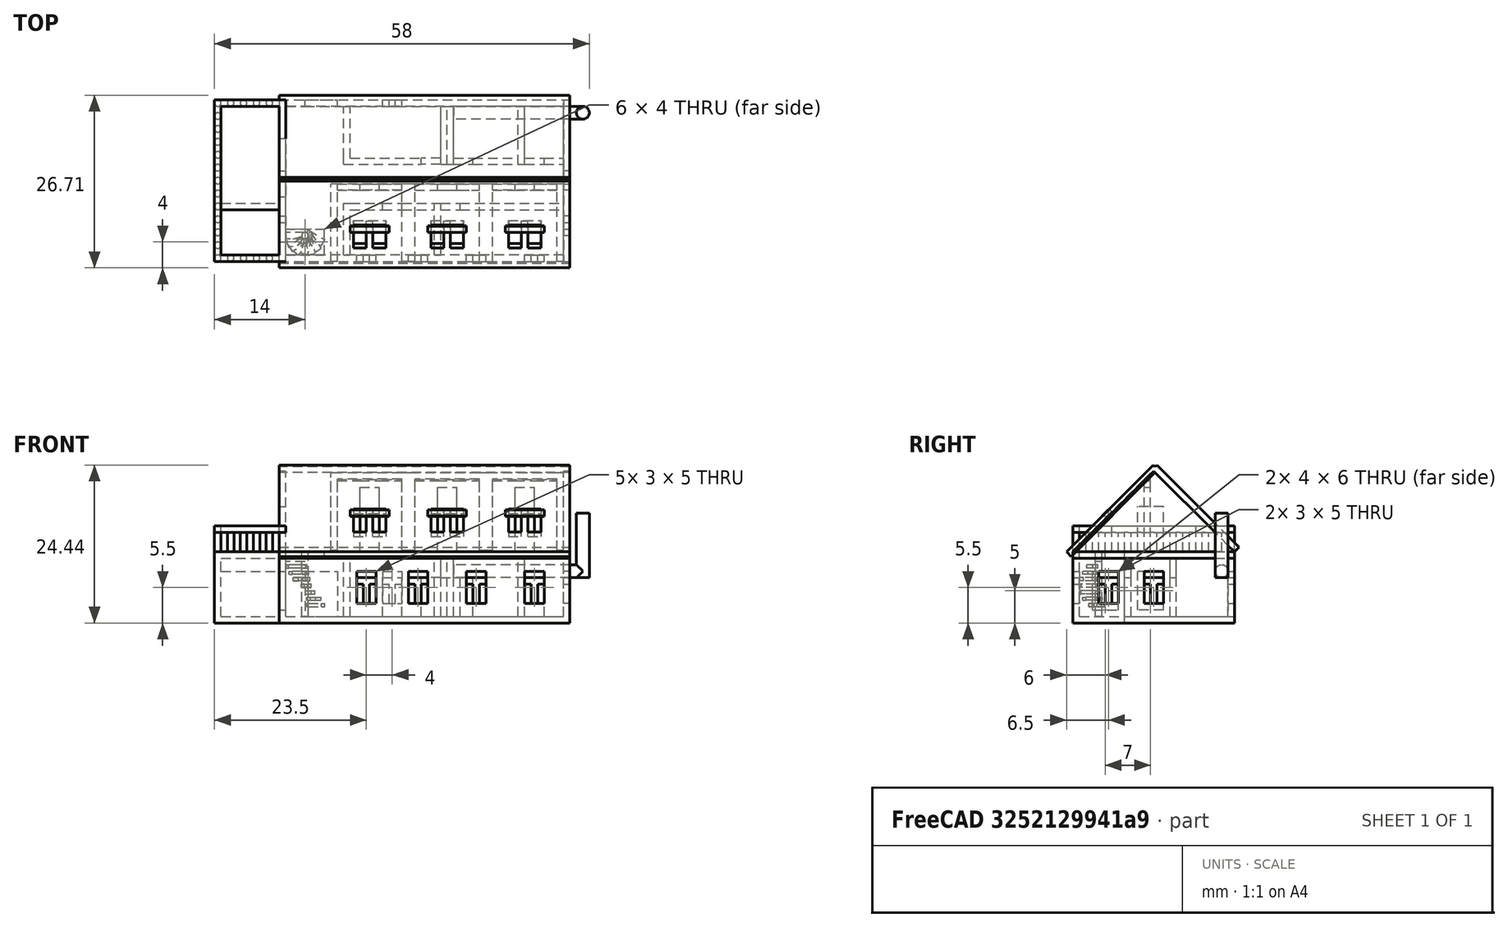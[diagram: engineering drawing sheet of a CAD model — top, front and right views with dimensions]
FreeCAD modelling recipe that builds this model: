
FCSTD DOCUMENT  (FreeCAD 0.18R4 (GitTag))
Label: House
License: All rights reserved
LicenseURL: http://en.wikipedia.org/wiki/All_rights_reserved
objects: Part::Box×102, Part::MultiFuse×56, Part::Cut×28, Part::Cylinder×25
note: 211 computed .brp shape members not serialized (recipe doc carries the construction recipe); baked Part::Feature solids carry a one-line shape summary decoded from their .brp

FEATURE [Part::Box] Box001  label="Куб001"
  AttacherType = Attacher::AttachEngine3D
  Height = 10
  Length = 45
  Width = 25
FEATURE [Part::Box] Box  label="Куб"
  AttacherType = Attacher::AttachEngine3D
  Height = 10
  Length = 43
  Placement = pos=(1,1,1) rot=(0,0,1;0rad)
  Width = 23
FEATURE [Part::Cut] Cut
  Base = -> Box001
  Tool = -> Box
FEATURE [Part::Box] Box002  label="Куб002"
  AttacherType = Attacher::AttachEngine3D
  Height = 9
  Length = 1
  Placement = pos=(16,15,1) rot=(0,0,1;0rad)
  Width = 9
FEATURE [Part::Box] Box003  label="Куб003"
  AttacherType = Attacher::AttachEngine3D
  Height = 9
  Length = 12
  Placement = pos=(1,15,1) rot=(0,0,1;0rad)
  Width = 1
FEATURE [Part::Box] Box004  label="Куб004"
  AttacherType = Attacher::AttachEngine3D
  Height = 3
  Length = 1
  Placement = pos=(16,15,7) rot=(0,0,1;1.5708rad)
  Width = 3
FEATURE [Part::Box] Box005  label="Куб005"
  AttacherType = Attacher::AttachEngine3D
  Height = 11
  Length = 8
  Placement = pos=(-9,0,0) rot=(0,0,1;1.5708rad)
  Width = 1
FEATURE [Part::Box] Box006  label="Куб006"
  AttacherType = Attacher::AttachEngine3D
  Height = 11
  Length = 9
  Placement = pos=(-9,0,0) rot=(0,0,1;0rad)
  Width = 1
FEATURE [Part::Box] Box007  label="Куб007"
  AttacherType = Attacher::AttachEngine3D
  Height = 9
  Length = 1
  Placement = pos=(10,1,1) rot=(0,0,1;0rad)
  Width = 8
FEATURE [Part::Box] Box008  label="Куб008"
  AttacherType = Attacher::AttachEngine3D
  Height = 9
  Length = 1
  Placement = pos=(24,1,1) rot=(0,0,1;0rad)
  Width = 8
FEATURE [Part::Box] Box009  label="Куб009"
  AttacherType = Attacher::AttachEngine3D
  Height = 9
  Length = 16
  Placement = pos=(28,8,1) rot=(0,0,1;0rad)
  Width = 1
FEATURE [Part::Box] Box010  label="Куб010"
  AttacherType = Attacher::AttachEngine3D
  Height = 3
  Length = 3
  Placement = pos=(25,8,7) rot=(0,0,1;0rad)
  Width = 1
FEATURE [Part::Box] Box011  label="Куб011"
  AttacherType = Attacher::AttachEngine3D
  Height = 9
  Length = 7
  Placement = pos=(37,15,1) rot=(0,0,1;0rad)
  Width = 1
FEATURE [Part::Box] Box012  label="Куб012"
  AttacherType = Attacher::AttachEngine3D
  Height = 9
  Length = 1
  Placement = pos=(33,15,1) rot=(0,0,1;0rad)
  Width = 9
FEATURE [Part::Box] Box013  label="Куб013"
  AttacherType = Attacher::AttachEngine3D
  Height = 3
  Length = 3
  Placement = pos=(34,15,7) rot=(0,0,1;0rad)
  Width = 1
FEATURE [Part::MultiFuse] Fusion003
  Placement = pos=(-7,0,0) rot=(0,0,1;0rad)
  Shapes = -> [Box013,Box012,Box011]
FEATURE [Part::MultiFuse] Fusion005
  Shapes = -> [Box010,Box008,Box009]
FEATURE [Part::Box] Box014  label="Куб014"
  AttacherType = Attacher::AttachEngine3D
  Height = 9
  Length = 3
  Placement = pos=(30,15,1) rot=(0,0,1;0rad)
  Width = 1
FEATURE [Part::Box] Box015  label="Куб015"
  AttacherType = Attacher::AttachEngine3D
  Height = 9
  Length = 1
  Placement = pos=(26,15,1) rot=(0,0,1;0rad)
  Width = 9
FEATURE [Part::Box] Box016  label="Куб016"
  AttacherType = Attacher::AttachEngine3D
  Height = 3
  Length = 3
  Placement = pos=(27,15,7) rot=(0,0,1;0rad)
  Width = 1
FEATURE [Part::Box] Box017  label="Куб017"
  AttacherType = Attacher::AttachEngine3D
  Height = 9
  Length = 5
  Placement = pos=(11,8,1) rot=(0,0,1;0rad)
  Width = 1
FEATURE [Part::Box] Box018  label="Куб018"
  AttacherType = Attacher::AttachEngine3D
  Height = 9
  Length = 5
  Placement = pos=(19,8,1) rot=(0,0,1;0rad)
  Width = 1
FEATURE [Part::Box] Box019  label="Куб019"
  AttacherType = Attacher::AttachEngine3D
  Height = 3
  Length = 3
  Placement = pos=(16,8,7) rot=(0,0,1;0rad)
  Width = 1
FEATURE [Part::MultiFuse] Fusion007
  Shapes = -> [Box019,Box018,Box017]
FEATURE [Part::Box] Box020  label="Куб020"
  AttacherType = Attacher::AttachEngine3D
  Height = 6
  Length = 6
  Placement = pos=(-2,10,2) rot=(0,0,1;0rad)
  Width = 4
FEATURE [Part::Cut] Cut001
  Base = -> Cut
  Tool = -> Box020
FEATURE [Part::Box] Box021  label="Куб021"
  AttacherType = Attacher::AttachEngine3D
  Height = 9
  Length = 10
  Placement = pos=(-10,8,0) rot=(0,0,1;0rad)
  Width = 1
FEATURE [Part::Box] Box022  label="Куб022"
  AttacherType = Attacher::AttachEngine3D
  Height = 9
  Length = 1
  Placement = pos=(-10,9,0) rot=(0,0,1;0rad)
  Width = 16
FEATURE [Part::Box] Box024  label="Куб024"
  AttacherType = Attacher::AttachEngine3D
  Height = 2
  Length = 9
  Placement = pos=(-9,24,7) rot=(0,0,1;0rad)
  Width = 1
FEATURE [Part::Box] Box025  label="Куб025"
  AttacherType = Attacher::AttachEngine3D
  Height = 1
  Length = 10
  Placement = pos=(-10,8,9) rot=(0,0,1;0rad)
  Width = 17
FEATURE [Part::MultiFuse] Fusion010
  Placement = pos=(0,0,1) rot=(0,0,1;0rad)
  Shapes = -> [Box025,Box024,Box022,Box021]
FEATURE [Part::Box] Box026  label="Куб026"
  AttacherType = Attacher::AttachEngine3D
  Height = 7
  Length = 5
  Placement = pos=(4,20,1) rot=(0,0,1;0rad)
  Width = 7
FEATURE [Part::MultiFuse] Fusion
  Placement = pos=(11,0,0) rot=(0,0,1;0rad)
  Shapes = -> [Box014,Box016,Box015]
FEATURE [Part::Box] Box027  label="Куб027"
  AttacherType = Attacher::AttachEngine3D
  Height = 1
  Length = 45
  Placement = pos=(0,0,10) rot=(0,0,1;0rad)
  Width = 25
FEATURE [Part::Box] Box028  label="Куб028"
  AttacherType = Attacher::AttachEngine3D
  Height = 13
  Length = 1
  Placement = pos=(0,0,11) rot=(0,0,1;0rad)
  Width = 25
FEATURE [Part::Box] Box029  label="Куб029"
  AttacherType = Attacher::AttachEngine3D
  Height = 10
  Length = 10
  Placement = pos=(-9,0,11) rot=(1,0,0;0.785398rad)
  Width = 20
FEATURE [Part::Box] Box030  label="Куб030"
  AttacherType = Attacher::AttachEngine3D
  Height = 20
  Length = 10
  Placement = pos=(-9,25,11) rot=(1,0,0;0.785398rad)
  Width = 10
FEATURE [Part::Cut] Cut003
  Base = -> Box028
  Tool = -> Box029
FEATURE [Part::Cut] Cut004
  Base = -> Cut003
  Tool = -> Box030
FEATURE [Part::Box] Box031  label="Куб031"
  AttacherType = Attacher::AttachEngine3D
  Height = 13
  Length = 1
  Placement = pos=(0,0,11) rot=(0,0,1;0rad)
  Width = 25
FEATURE [Part::Box] Box032  label="Куб032"
  AttacherType = Attacher::AttachEngine3D
  Height = 10
  Length = 10
  Placement = pos=(-9,0,11) rot=(1,0,0;0.785398rad)
  Width = 20
FEATURE [Part::Box] Box033  label="Куб033"
  AttacherType = Attacher::AttachEngine3D
  Height = 20
  Length = 10
  Placement = pos=(-9,25,11) rot=(1,0,0;0.785398rad)
  Width = 10
FEATURE [Part::Box] Box034  label="Куб034"
  AttacherType = Attacher::AttachEngine3D
  Height = 19
  Length = 45
  Placement = pos=(0,-1,11) rot=(-1,0,0;0.785398rad)
  Width = 1
FEATURE [Part::Box] Box035  label="Куб035"
  AttacherType = Attacher::AttachEngine3D
  Height = 18
  Length = 45
  Placement = pos=(0,25,11) rot=(1,0,0;0.785398rad)
  Width = 1
FEATURE [Part::Box] Box036  label="Куб036"
  AttacherType = Attacher::AttachEngine3D
  Height = 1
  Length = 6
  Placement = pos=(1,1,10) rot=(0,0,1;0rad)
  Width = 4
FEATURE [Part::Box] Box052  label="Куб052"
  AttacherType = Attacher::AttachEngine3D
  Height = 1
  Length = 10
  Placement = pos=(-10,8,0) rot=(0,0,1;0rad)
  Width = 17
FEATURE [Part::MultiFuse] Fusion024
  Shapes = -> [Fusion010,Box052]
FEATURE [Part::Box] Box056  label="Куб056"
  AttacherType = Attacher::AttachEngine3D
  Height = 5
  Length = 3
  Placement = pos=(16,20,3) rot=(0,0,1;0rad)
  Width = 6
FEATURE [Part::Box] Box058  label="Куб058"
  AttacherType = Attacher::AttachEngine3D
  Height = 5
  Length = 3
  Placement = pos=(12,-2,3) rot=(0,0,1;0rad)
  Width = 6
FEATURE [Part::Box] Box059  label="Куб059"
  AttacherType = Attacher::AttachEngine3D
  Height = 5
  Length = 3
  Placement = pos=(20,-2,3) rot=(0,0,1;0rad)
  Width = 6
FEATURE [Part::Box] Box060  label="Куб060"
  AttacherType = Attacher::AttachEngine3D
  Height = 5
  Length = 3
  Placement = pos=(29,-2,3) rot=(0,0,1;0rad)
  Width = 6
FEATURE [Part::Box] Box061  label="Куб061"
  AttacherType = Attacher::AttachEngine3D
  Height = 5
  Length = 3
  Placement = pos=(38,-2,3) rot=(0,0,1;0rad)
  Width = 6
FEATURE [Part::Box] Box062  label="Куб062"
  AttacherType = Attacher::AttachEngine3D
  Height = 5
  Length = 3
  Placement = pos=(46,4,3) rot=(0,0,1;1.5708rad)
  Width = 6
FEATURE [Part::Box] Box063  label="Куб063"
  AttacherType = Attacher::AttachEngine3D
  Height = 5
  Length = 3
  Placement = pos=(46,11,3) rot=(0,0,1;1.5708rad)
  Width = 6
FEATURE [Part::Cylinder] Cylinder001  label="Цилиндр001"
  Angle = 360
  AttacherType = Attacher::AttachEngine3D
  Height = 21
  Placement = pos=(48,23,8) rot=(0,-1,0;1.5708rad)
  Radius = 1
FEATURE [Part::Cylinder] Cylinder002  label="Цилиндр002"
  Angle = 360
  AttacherType = Attacher::AttachEngine3D
  Height = 9
  Placement = pos=(47,23,7) rot=(0,0,1;0rad)
  Radius = 1
FEATURE [Part::Cylinder] Cylinder003  label="Цилиндр003"
  Angle = 360
  AttacherType = Attacher::AttachEngine3D
  Height = 10
  Placement = pos=(47,23,7) rot=(0,0,1;0rad)
  Radius = 1
FEATURE [Part::Cut] Cut021
  Base = -> Cylinder001
  Tool = -> Cylinder002
FEATURE [Part::Box] Box064  label="Куб064"
  AttacherType = Attacher::AttachEngine3D
  Height = 10
  Length = 10
  Placement = pos=(47,14,0) rot=(0,0,1;0rad)
  Width = 10
FEATURE [Part::Cut] Cut022
  Base = -> Cut021
  Tool = -> Box064
FEATURE [Part::MultiFuse] Fusion025
  Shapes = -> [Cylinder003,Cut022]
FEATURE [Part::Box] Box066  label="Куб066"
  AttacherType = Attacher::AttachEngine3D
  Height = 1
  Length = 3
  Placement = pos=(12,0,6) rot=(0,0,1;0rad)
  Width = 1
FEATURE [Part::Box] Box067  label="Куб067"
  AttacherType = Attacher::AttachEngine3D
  Height = 1
  Length = 3
  Placement = pos=(20,0,6) rot=(0,0,1;0rad)
  Width = 1
FEATURE [Part::Box] Box068  label="Куб068"
  AttacherType = Attacher::AttachEngine3D
  Height = 1
  Length = 3
  Placement = pos=(29,0,6) rot=(0,0,1;0rad)
  Width = 1
FEATURE [Part::Box] Box069  label="Куб069"
  AttacherType = Attacher::AttachEngine3D
  Height = 1
  Length = 3
  Placement = pos=(38,0,6) rot=(0,0,1;0rad)
  Width = 1
FEATURE [Part::Box] Box071  label="Куб071"
  AttacherType = Attacher::AttachEngine3D
  Height = 3
  Length = 1
  Placement = pos=(13,0,3) rot=(0,0,1;0rad)
  Width = 1
FEATURE [Part::Box] Box072  label="Куб072"
  AttacherType = Attacher::AttachEngine3D
  Height = 3
  Length = 1
  Placement = pos=(21,0,3) rot=(0,0,1;0rad)
  Width = 1
FEATURE [Part::Box] Box073  label="Куб073"
  AttacherType = Attacher::AttachEngine3D
  Height = 3
  Length = 1
  Placement = pos=(30,0,3) rot=(0,0,1;0rad)
  Width = 1
FEATURE [Part::Box] Box074  label="Куб074"
  AttacherType = Attacher::AttachEngine3D
  Height = 3
  Length = 1
  Placement = pos=(39,0,3) rot=(0,0,1;0rad)
  Width = 1
FEATURE [Part::Box] Box078  label="Куб078"
  AttacherType = Attacher::AttachEngine3D
  Height = 1
  Length = 1
  Placement = pos=(44,4,6) rot=(0,0,1;0rad)
  Width = 3
FEATURE [Part::Box] Box079  label="Куб079"
  AttacherType = Attacher::AttachEngine3D
  Height = 3
  Length = 1
  Placement = pos=(44,12,3) rot=(0,0,1;0rad)
  Width = 1
FEATURE [Part::Box] Box080  label="Куб080"
  AttacherType = Attacher::AttachEngine3D
  Height = 3
  Length = 1
  Placement = pos=(44,5,3) rot=(0,0,1;0rad)
  Width = 1
FEATURE [Part::Box] Box081  label="Куб081"
  AttacherType = Attacher::AttachEngine3D
  Height = 1
  Length = 1
  Placement = pos=(44,11,6) rot=(0,0,1;0rad)
  Width = 3
FEATURE [Part::MultiFuse] Fusion030
  Placement = pos=(9,0,0) rot=(0,0,1;0rad)
  Shapes = -> [Box004,Box002,Box003]
FEATURE [Part::MultiFuse] Fusion033
  Shapes = -> [Box069,Box074]
FEATURE [Part::MultiFuse] Fusion034
  Shapes = -> [Box068,Box073]
FEATURE [Part::MultiFuse] Fusion035
  Shapes = -> [Box080,Box078]
FEATURE [Part::MultiFuse] Fusion036
  Shapes = -> [Box081,Box079]
FEATURE [Part::MultiFuse] Fusion037
  Shapes = -> [Box072,Box067]
FEATURE [Part::Cut] Cut029
  Base = -> Cut001
  Tool = -> Box026
FEATURE [Part::Cut] Cut030
  Base = -> Cut029
  Tool = -> Box056
FEATURE [Part::Box] Box097  label="Куб097"
  AttacherType = Attacher::AttachEngine3D
  Height = 1
  Length = 3
  Placement = pos=(20,0,6) rot=(0,0,1;0rad)
  Width = 1
FEATURE [Part::Box] Box098  label="Куб098"
  AttacherType = Attacher::AttachEngine3D
  Height = 3
  Length = 1
  Placement = pos=(21,0,3) rot=(0,0,1;0rad)
  Width = 1
FEATURE [Part::MultiFuse] Fusion038
  Placement = pos=(-4,24,0) rot=(0,0,1;0rad)
  Shapes = -> [Box098,Box097]
FEATURE [Part::Box] Box099  label="Куб099"
  AttacherType = Attacher::AttachEngine3D
  Height = 9
  Length = 1
  Placement = pos=(10,16,1) rot=(0,0,1;0rad)
  Width = 8
FEATURE [Part::MultiFuse] Fusion039
  Shapes = -> [Box099,Fusion030]
FEATURE [Part::MultiFuse] Fusion040
  Shapes = -> [Box007,Fusion007]
FEATURE [Part::Box] Box100  label="Куб100"
  AttacherType = Attacher::AttachEngine3D
  Height = 1
  Length = 9
  Placement = pos=(-9,1,10) rot=(0,0,1;0rad)
  Width = 7
FEATURE [Part::MultiFuse] Fusion041
  Shapes = -> [Box100,Box006]
FEATURE [Part::MultiFuse] Fusion042
  Shapes = -> [Fusion041,Box005]
FEATURE [Part::Box] Box101  label="Куб101"
  AttacherType = Attacher::AttachEngine3D
  Height = 6
  Length = 3
  Placement = pos=(0,3,2) rot=(0,0,1;0rad)
  Width = 4
FEATURE [Part::Box] Box102  label="Куб102"
  AttacherType = Attacher::AttachEngine3D
  Height = 1
  Length = 9
  Placement = pos=(-9,0,0) rot=(0,0,1;0rad)
  Width = 8
FEATURE [Part::MultiFuse] Fusion043
  Shapes = -> [Fusion042,Box102]
FEATURE [Part::Cylinder] Cylinder005  label="Цилиндр005"
  Angle = 360
  AttacherType = Attacher::AttachEngine3D
  Height = 10
  Placement = pos=(4,4,1) rot=(0,0,1;0rad)
  Radius = 0.5
FEATURE [Part::Box] Box103  label="Куб103"
  AttacherType = Attacher::AttachEngine3D
  Height = 0.5
  Length = 3
  Placement = pos=(4,4,2.5) rot=(0,0,-1;0.541052rad)
  Width = 1
FEATURE [Part::Box] Box104  label="Куб104"
  AttacherType = Attacher::AttachEngine3D
  Height = 0.5
  Length = 3
  Placement = pos=(4,4,3.5) rot=(0,0,-1;0.994838rad)
  Width = 1
FEATURE [Part::Box] Box105  label="Куб105"
  AttacherType = Attacher::AttachEngine3D
  Height = 0.5
  Length = 3
  Placement = pos=(4,4,4.5) rot=(0,0,-1;1.39626rad)
  Width = 1
FEATURE [Part::Box] Box106  label="Куб106"
  AttacherType = Attacher::AttachEngine3D
  Height = 0.5
  Length = 2.75
  Placement = pos=(4,4,5.5) rot=(0,0,-1;1.78024rad)
  Width = 1
FEATURE [Part::Box] Box107  label="Куб107"
  AttacherType = Attacher::AttachEngine3D
  Height = 0.5
  Length = 3
  Placement = pos=(4,4,6.5) rot=(0,0,1;4.06662rad)
  Width = 1
FEATURE [Part::Box] Box108  label="Куб108"
  AttacherType = Attacher::AttachEngine3D
  Height = 0.5
  Length = 3
  Placement = pos=(4,4,7.5) rot=(0,0,1;3.73501rad)
  Width = 1
FEATURE [Part::Box] Box109  label="Куб109"
  AttacherType = Attacher::AttachEngine3D
  Height = 0.5
  Length = 3
  Placement = pos=(4,4,8.5) rot=(0,0,1;3.45575rad)
  Width = 1
FEATURE [Part::Box] Box110  label="Куб110"
  AttacherType = Attacher::AttachEngine3D
  Height = 0.5
  Length = 3
  Placement = pos=(4,4.5,9.5) rot=(0,0,1;3.14159rad)
  Width = 1
FEATURE [Part::Cut] Cut031
  Base = -> Cut030
  Tool = -> Box059
FEATURE [Part::Cut] Cut032
  Base = -> Cut031
  Tool = -> Box058
FEATURE [Part::Cut] Cut033
  Base = -> Cut032
  Tool = -> Box062
FEATURE [Part::Cut] Cut034
  Base = -> Cut033
  Tool = -> Box063
FEATURE [Part::Cut] Cut035
  Base = -> Cut034
  Tool = -> Box061
FEATURE [Part::Cut] Cut036
  Base = -> Cut035
  Tool = -> Box060
FEATURE [Part::Cut] Cut037
  Base = -> Cut036
  Tool = -> Box101
FEATURE [Part::Cut] Cut038
  Base = -> Box027
  Tool = -> Box036
FEATURE [Part::MultiFuse] Fusion044
  Shapes = -> [Cylinder005,Box110]
FEATURE [Part::MultiFuse] Fusion045
  Shapes = -> [Fusion044,Box109]
FEATURE [Part::MultiFuse] Fusion046
  Shapes = -> [Fusion045,Box108]
FEATURE [Part::MultiFuse] Fusion047
  Shapes = -> [Fusion046,Box107]
FEATURE [Part::MultiFuse] Fusion048
  Shapes = -> [Fusion047,Box106]
FEATURE [Part::MultiFuse] Fusion049
  Shapes = -> [Fusion048,Box105]
FEATURE [Part::MultiFuse] Fusion050
  Shapes = -> [Fusion049,Box104]
FEATURE [Part::MultiFuse] Fusion051
  Shapes = -> [Fusion050,Box103]
FEATURE [Part::Cut] Cut005
  Base = -> Box031
  Tool = -> Box032
FEATURE [Part::Cut] Cut006
  Base = -> Cut005
  Placement = pos=(44,0,0) rot=(0,0,1;0rad)
  Tool = -> Box033
FEATURE [Part::Box] Box111  label="Куб111"
  AttacherType = Attacher::AttachEngine3D
  Height = 7
  Length = 5
  Placement = pos=(-1,10,11) rot=(0,0,1;0rad)
  Width = 4
FEATURE [Part::Cut] Cut041
  Base = -> Cut004
  Tool = -> Box111
FEATURE [Part::Box] Box112  label="Куб112"
  AttacherType = Attacher::AttachEngine3D
  Height = 1
  Length = 1
  Placement = pos=(-10,0,14) rot=(0,0,1;0rad)
  Width = 25
FEATURE [Part::Cylinder] Cylinder006  label="Цилиндр006"
  Angle = 360
  AttacherType = Attacher::AttachEngine3D
  Height = 3
  Placement = pos=(-9.5,0.5,11) rot=(0,0,1;0rad)
  Radius = 0.5
FEATURE [Part::Cylinder] Cylinder007  label="Цилиндр007"
  Angle = 360
  AttacherType = Attacher::AttachEngine3D
  Height = 3
  Placement = pos=(-9.5,2.5,11) rot=(0,0,1;0rad)
  Radius = 0.5
FEATURE [Part::Cylinder] Cylinder008  label="Цилиндр008"
  Angle = 360
  AttacherType = Attacher::AttachEngine3D
  Height = 3
  Placement = pos=(-9.5,4.5,11) rot=(0,0,1;0rad)
  Radius = 0.5
FEATURE [Part::Cylinder] Cylinder009  label="Цилиндр009"
  Angle = 360
  AttacherType = Attacher::AttachEngine3D
  Height = 3
  Placement = pos=(-9.5,6.5,11) rot=(0,0,1;0rad)
  Radius = 0.5
FEATURE [Part::Cylinder] Cylinder010  label="Цилиндр010"
  Angle = 360
  AttacherType = Attacher::AttachEngine3D
  Height = 3
  Placement = pos=(-9.5,8.5,11) rot=(0,0,1;0rad)
  Radius = 0.5
FEATURE [Part::Cylinder] Cylinder011  label="Цилиндр011"
  Angle = 360
  AttacherType = Attacher::AttachEngine3D
  Height = 3
  Placement = pos=(-9.5,10.5,11) rot=(0,0,1;0rad)
  Radius = 0.5
FEATURE [Part::Cylinder] Cylinder012  label="Цилиндр012"
  Angle = 360
  AttacherType = Attacher::AttachEngine3D
  Height = 3
  Placement = pos=(-9.5,12.5,11) rot=(0,0,1;0rad)
  Radius = 0.5
FEATURE [Part::Cylinder] Cylinder013  label="Цилиндр013"
  Angle = 360
  AttacherType = Attacher::AttachEngine3D
  Height = 3
  Placement = pos=(-9.5,14.5,11) rot=(0,0,1;0rad)
  Radius = 0.5
FEATURE [Part::Cylinder] Cylinder014  label="Цилиндр014"
  Angle = 360
  AttacherType = Attacher::AttachEngine3D
  Height = 3
  Placement = pos=(-9.5,16.5,11) rot=(0,0,1;0rad)
  Radius = 0.5
FEATURE [Part::Cylinder] Cylinder015  label="Цилиндр015"
  Angle = 360
  AttacherType = Attacher::AttachEngine3D
  Height = 3
  Placement = pos=(-9.5,18.5,11) rot=(0,0,1;0rad)
  Radius = 0.5
FEATURE [Part::Cylinder] Cylinder016  label="Цилиндр016"
  Angle = 360
  AttacherType = Attacher::AttachEngine3D
  Height = 3
  Placement = pos=(-9.5,20.5,11) rot=(0,0,1;0rad)
  Radius = 0.5
FEATURE [Part::Cylinder] Cylinder017  label="Цилиндр017"
  Angle = 360
  AttacherType = Attacher::AttachEngine3D
  Height = 3
  Placement = pos=(-9.5,22.5,11) rot=(0,0,1;0rad)
  Radius = 0.5
FEATURE [Part::Cylinder] Cylinder018  label="Цилиндр018"
  Angle = 360
  AttacherType = Attacher::AttachEngine3D
  Height = 3
  Placement = pos=(-9.5,24.5,11) rot=(0,0,1;0rad)
  Radius = 0.5
FEATURE [Part::MultiFuse] Fusion053
  Shapes = -> [Cylinder006,Cylinder007,Cylinder009,Cylinder008,Cylinder010,Cylinder011,Cylinder013,Cylinder012,Cylinder014,Cylinder015,Cylinder016,Cylinder017,Cylinder018]
FEATURE [Part::Box] Box113  label="Куб113"
  AttacherType = Attacher::AttachEngine3D
  Height = 1
  Length = 9
  Placement = pos=(-9,0,14) rot=(0,0,1;0rad)
  Width = 1
FEATURE [Part::MultiFuse] Fusion054
  Shapes = -> [Box112,Fusion053]
FEATURE [Part::Cylinder] Cylinder019  label="Цилиндр019"
  Angle = 360
  AttacherType = Attacher::AttachEngine3D
  Height = 3
  Placement = pos=(-5.5,0.5,11) rot=(0,0,1;0rad)
  Radius = 0.5
FEATURE [Part::Cylinder] Cylinder020  label="Цилиндр020"
  Angle = 360
  AttacherType = Attacher::AttachEngine3D
  Height = 3
  Placement = pos=(-7.5,0.5,11) rot=(0,0,1;0rad)
  Radius = 0.5
FEATURE [Part::Cylinder] Cylinder021  label="Цилиндр021"
  Angle = 360
  AttacherType = Attacher::AttachEngine3D
  Height = 3
  Placement = pos=(-1.5,0.5,11) rot=(0,0,1;0rad)
  Radius = 0.5
FEATURE [Part::Cylinder] Cylinder022  label="Цилиндр022"
  Angle = 360
  AttacherType = Attacher::AttachEngine3D
  Height = 3
  Placement = pos=(-3.5,0.5,11) rot=(0,0,1;0rad)
  Radius = 0.5
FEATURE [Part::MultiFuse] Fusion055
  Shapes = -> [Cylinder022,Cylinder021,Cylinder020,Cylinder019]
FEATURE [Part::Box] Box114  label="Куб114"
  AttacherType = Attacher::AttachEngine3D
  Height = 1
  Length = 9
  Placement = pos=(-9,24,14) rot=(0,0,1;0rad)
  Width = 1
FEATURE [Part::Cylinder] Cylinder023  label="Цилиндр023"
  Angle = 360
  AttacherType = Attacher::AttachEngine3D
  Height = 3
  Placement = pos=(-7.5,0.5,11) rot=(0,0,1;0rad)
  Radius = 0.5
FEATURE [Part::Cylinder] Cylinder024  label="Цилиндр024"
  Angle = 360
  AttacherType = Attacher::AttachEngine3D
  Height = 3
  Placement = pos=(-5.5,0.5,11) rot=(0,0,1;0rad)
  Radius = 0.5
FEATURE [Part::Cylinder] Cylinder025  label="Цилиндр025"
  Angle = 360
  AttacherType = Attacher::AttachEngine3D
  Height = 3
  Placement = pos=(-1.5,0.5,11) rot=(0,0,1;0rad)
  Radius = 0.5
FEATURE [Part::Cylinder] Cylinder026  label="Цилиндр026"
  Angle = 360
  AttacherType = Attacher::AttachEngine3D
  Height = 3
  Placement = pos=(-3.5,0.5,11) rot=(0,0,1;0rad)
  Radius = 0.5
FEATURE [Part::MultiFuse] Fusion056
  Placement = pos=(0,24,0) rot=(0,0,1;0rad)
  Shapes = -> [Cylinder026,Cylinder025,Cylinder023,Cylinder024]
FEATURE [Part::MultiFuse] Fusion057
  Shapes = -> [Fusion056,Box114]
FEATURE [Part::MultiFuse] Fusion058
  Shapes = -> [Box113,Fusion055]
FEATURE [Part::MultiFuse] Fusion059
  Shapes = -> [Box035,Box034]
FEATURE [Part::Box] Box115  label="Куб115"
  AttacherType = Attacher::AttachEngine3D
  Height = 1
  Length = 1
  Placement = pos=(0,0,14) rot=(0,0,1;0rad)
  Width = 6
FEATURE [Part::MultiFuse] Fusion060
  Shapes = -> [Fusion054,Fusion057,Fusion058]
FEATURE [Part::Box] Box116  label="Куб116"
  AttacherType = Attacher::AttachEngine3D
  Height = 1
  Length = 1
  Placement = pos=(0,19,14) rot=(0,0,1;0rad)
  Width = 6
FEATURE [Part::MultiFuse] Fusion061
  Shapes = -> [Box116,Box115]
FEATURE [Part::MultiFuse] Fusion062
  Shapes = -> [Fusion061,Fusion060]
FEATURE [Part::Box] Box121  label="Куб121"
  AttacherType = Attacher::AttachEngine3D
  Height = 17
  Length = 1
  Placement = pos=(35,0,11) rot=(0,0,1;0rad)
  Width = 12
FEATURE [Part::Box] Box124  label="Куб124"
  AttacherType = Attacher::AttachEngine3D
  Height = 23
  Length = 18
  Placement = pos=(25,-11.36,22.5) rot=(-1,0,0;0.785398rad)
  Width = 16
FEATURE [Part::Cut] Cut042
  Base = -> Box121
  Placement = pos=(-2,0,0) rot=(0,0,1;0rad)
  Tool = -> Box124
FEATURE [Part::Box] Box125  label="Куб125"
  AttacherType = Attacher::AttachEngine3D
  Height = 23
  Length = 18
  Placement = pos=(25,-11.36,22.5) rot=(-1,0,0;0.785398rad)
  Width = 16
FEATURE [Part::Box] Box126  label="Куб126"
  AttacherType = Attacher::AttachEngine3D
  Height = 17
  Length = 1
  Placement = pos=(35,0,11) rot=(0,0,1;0rad)
  Width = 12
FEATURE [Part::Cut] Cut043
  Base = -> Box126
  Placement = pos=(-13,0,0) rot=(0,0,1;0rad)
  Tool = -> Box125
FEATURE [Part::Cut] Cut044
FEATURE [Part::MultiFuse] Fusion063
  Placement = pos=(-2,0,0) rot=(0,0,1;0rad)
  Shapes = -> [Cut042,Cut043,Cut044]
FEATURE [Part::MultiFuse] Fusion064
  Placement = pos=(10,0,0) rot=(0,0,1;0rad)
  Shapes = -> [Cut042,Cut043,Cut044]
FEATURE [Part::MultiFuse] Fusion065
  Placement = pos=(-14,0,0) rot=(0,0,1;0rad)
  Shapes = -> [Cut042,Cut043,Cut044]
FEATURE [Part::MultiFuse] Fusion066
  Shapes = -> [Cut006,Cut041]
FEATURE [Part::Box] Box129  label="Куб129"
  AttacherType = Attacher::AttachEngine3D
  Height = 5
  Length = 5
  Placement = pos=(23.5,-6.36,22.5) rot=(-1,0,0;0.785398rad)
  Width = 16
FEATURE [Part::Box] Box130  label="Куб130"
  AttacherType = Attacher::AttachEngine3D
  Height = 5
  Length = 5
  Placement = pos=(35.5,-6.36,22.5) rot=(-1,0,0;0.785398rad)
  Width = 16
FEATURE [Part::Box] Box131  label="Куб131"
  AttacherType = Attacher::AttachEngine3D
  Height = 5
  Length = 5
  Placement = pos=(11.5,-6.36,22.5) rot=(-1,0,0;0.785398rad)
  Width = 16
FEATURE [Part::Cut] Cut046
  Base = -> Fusion059
  Tool = -> Box129
FEATURE [Part::Cut] Cut047
  Base = -> Cut046
  Tool = -> Box131
FEATURE [Part::Cut] Cut048
  Base = -> Cut047
  Tool = -> Box130
FEATURE [Part::Box] Box136  label="Куб136"
  AttacherType = Attacher::AttachEngine3D
  Height = 23
  Length = 12
  Placement = pos=(22,-11.36,22.5) rot=(-1,0,0;0.785398rad)
  Width = 16
FEATURE [Part::Box] Box137  label="Куб137"
  AttacherType = Attacher::AttachEngine3D
  Height = 1
  Length = 6
  Placement = pos=(23,11,22.2) rot=(0,0,1;0rad)
  Width = 1
FEATURE [Part::Cut] Cut051
  Base = -> Box137
  Placement = pos=(-12,-6.5,-5.7) rot=(0,0,1;0rad)
  Tool = -> Box136
FEATURE [Part::Box] Box138  label="Куб138"
  AttacherType = Attacher::AttachEngine3D
  Height = 5
  Length = 1
  Placement = pos=(13.5,2,14) rot=(-1,0,0;0.785398rad)
  Width = 1
FEATURE [Part::MultiFuse] Fusion067
  Shapes = -> [Box138,Cut051]
FEATURE [Part::Box] Box139  label="Куб139"
  AttacherType = Attacher::AttachEngine3D
  Height = 23
  Length = 12
  Placement = pos=(22,-11.36,22.5) rot=(-1,0,0;0.785398rad)
  Width = 16
FEATURE [Part::Box] Box140  label="Куб140"
  AttacherType = Attacher::AttachEngine3D
  Height = 5
  Length = 1
  Placement = pos=(13.5,2,14) rot=(-1,0,0;0.785398rad)
  Width = 1
FEATURE [Part::Box] Box141  label="Куб141"
  AttacherType = Attacher::AttachEngine3D
  Height = 1
  Length = 6
  Placement = pos=(23,11,22.2) rot=(0,0,1;0rad)
  Width = 1
FEATURE [Part::Cut] Cut052
  Base = -> Box141
  Placement = pos=(-12,-6.5,-5.7) rot=(0,0,1;0rad)
  Tool = -> Box139
FEATURE [Part::MultiFuse] Fusion068
  Placement = pos=(12,0,0) rot=(0,0,1;0rad)
  Shapes = -> [Box140,Cut052]
FEATURE [Part::Box] Box142  label="Куб142"
  AttacherType = Attacher::AttachEngine3D
  Height = 23
  Length = 12
  Placement = pos=(22,-11.36,22.5) rot=(-1,0,0;0.785398rad)
  Width = 16
FEATURE [Part::Box] Box143  label="Куб143"
  AttacherType = Attacher::AttachEngine3D
  Height = 5
  Length = 1
  Placement = pos=(13.5,2,14) rot=(-1,0,0;0.785398rad)
  Width = 1
FEATURE [Part::Box] Box144  label="Куб144"
  AttacherType = Attacher::AttachEngine3D
  Height = 1
  Length = 6
  Placement = pos=(23,11,22.2) rot=(0,0,1;0rad)
  Width = 1
FEATURE [Part::Cut] Cut053
  Base = -> Box144
  Placement = pos=(-12,-6.5,-5.7) rot=(0,0,1;0rad)
  Tool = -> Box142
FEATURE [Part::MultiFuse] Fusion069
  Placement = pos=(24,0,0) rot=(0,0,1;0rad)
  Shapes = -> [Box143,Cut053]
FEATURE [Part::MultiFuse] Fusion070
  Shapes = -> [Fusion069,Fusion068,Fusion067,Cut048]
FEATURE [Part::Box] Box145  label="Куб145"
  AttacherType = Attacher::AttachEngine3D
  Height = 11
  Length = 3.5
  Placement = pos=(9,11,11) rot=(0,0,1;0rad)
  Width = 1
FEATURE [Part::Box] Box146  label="Куб146"
  AttacherType = Attacher::AttachEngine3D
  Height = 11
  Length = 3.5
  Placement = pos=(15.5,11,11) rot=(0,0,1;0rad)
  Width = 1
FEATURE [Part::Box] Box147  label="Куб147"
  AttacherType = Attacher::AttachEngine3D
  Height = 1
  Length = 3
  Placement = pos=(12.5,11,21) rot=(0,0,1;0rad)
  Width = 1
FEATURE [Part::MultiFuse] Fusion071
  Shapes = -> [Box146,Box145]
FEATURE [Part::MultiFuse] Fusion072
  Shapes = -> [Box147,Fusion071]
FEATURE [Part::Box] Box148  label="Куб148"
  AttacherType = Attacher::AttachEngine3D
  Height = 11
  Length = 3.5
  Placement = pos=(15.5,11,11) rot=(0,0,1;0rad)
  Width = 1
FEATURE [Part::Box] Box149  label="Куб149"
  AttacherType = Attacher::AttachEngine3D
  Height = 1
  Length = 3
  Placement = pos=(12.5,11,21) rot=(0,0,1;0rad)
  Width = 1
FEATURE [Part::Box] Box150  label="Куб150"
  AttacherType = Attacher::AttachEngine3D
  Height = 11
  Length = 3.5
  Placement = pos=(9,11,11) rot=(0,0,1;0rad)
  Width = 1
FEATURE [Part::MultiFuse] Fusion074
  Shapes = -> [Box148,Box150]
FEATURE [Part::MultiFuse] Fusion073
  Placement = pos=(12,0,0) rot=(0,0,1;0rad)
  Shapes = -> [Box149,Fusion074]
FEATURE [Part::Box] Box151  label="Куб151"
  AttacherType = Attacher::AttachEngine3D
  Height = 11
  Length = 3.5
  Placement = pos=(15.5,11,11) rot=(0,0,1;0rad)
  Width = 1
FEATURE [Part::Box] Box152  label="Куб152"
  AttacherType = Attacher::AttachEngine3D
  Height = 1
  Length = 3
  Placement = pos=(12.5,11,21) rot=(0,0,1;0rad)
  Width = 1
FEATURE [Part::Box] Box153  label="Куб153"
  AttacherType = Attacher::AttachEngine3D
  Height = 11
  Length = 3.5
  Placement = pos=(9,11,11) rot=(0,0,1;0rad)
  Width = 1
FEATURE [Part::MultiFuse] Fusion076
  Shapes = -> [Box151,Box153]
FEATURE [Part::MultiFuse] Fusion075
  Placement = pos=(24,0,0) rot=(0,0,1;0rad)
  Shapes = -> [Box152,Fusion076]
FEATURE [Part::MultiFuse] Fusion077
  Shapes = -> [Fusion063,Fusion073]
FEATURE [Part::MultiFuse] Fusion078
  Shapes = -> [Fusion075,Fusion064]
FEATURE [Part::MultiFuse] Fusion079
  Shapes = -> [Fusion065,Fusion072]
FEATURE [Part::MultiFuse] Fusion080
  Shapes = -> [Fusion077,Fusion078,Fusion079]
FEATURE [Part::MultiFuse] Fusion081
  Shapes = -> [Box066,Box071]
